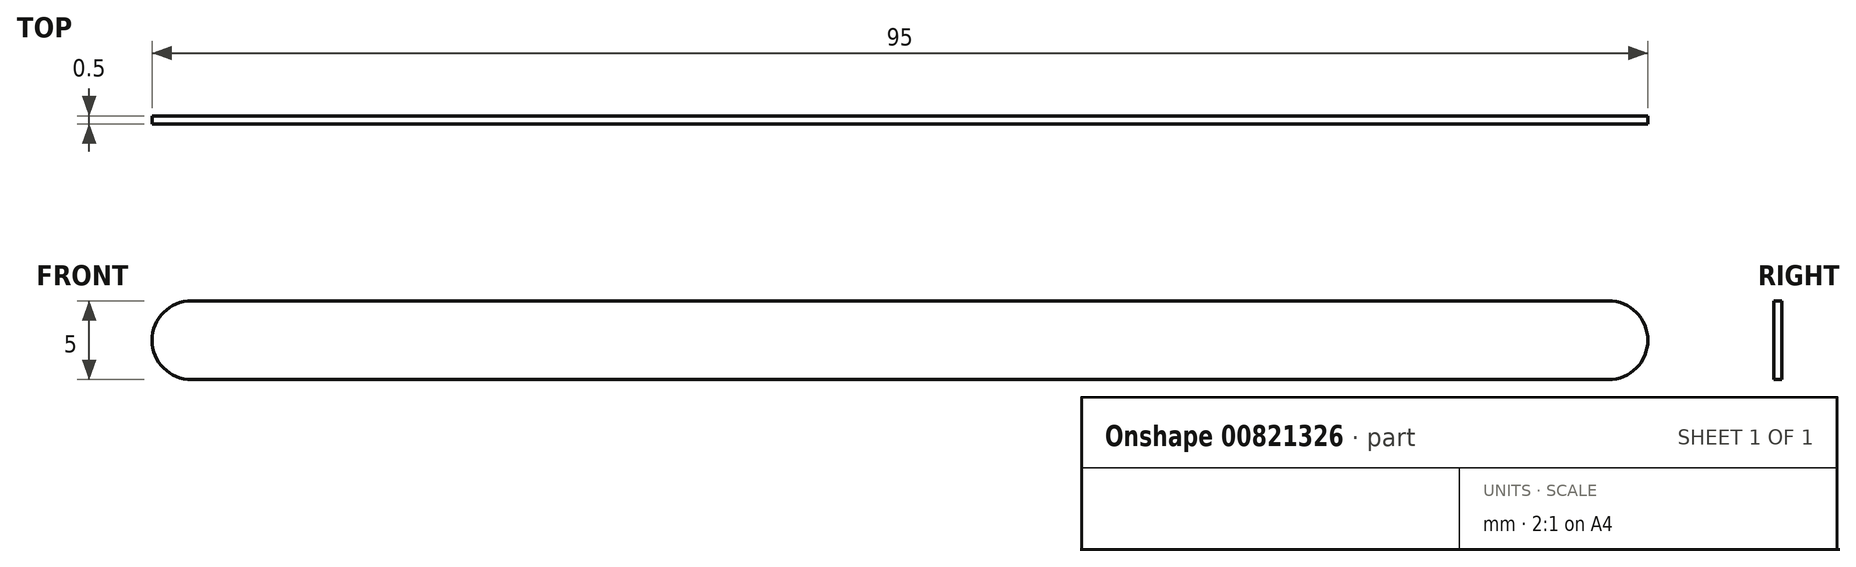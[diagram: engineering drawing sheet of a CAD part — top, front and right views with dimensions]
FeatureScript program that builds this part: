
annotation { "Feature Type Name" : "Feature", "Feature Type Description" : "" }
export const myFeature = defineFeature(function(context is Context, id is Id, definition is map)
    precondition{}
    {
        {
            var Q0;
            Q0=qCreatedBy(makeId("Front.planeOp"),FACE);
            var sketch = newSketch(context, id + "F0", { "sketchPlane" : qUnion([Q0])});
            skLineSegment(sketch, "E0", {"start": v(-26.27, 0) * mm, "end": v(63.73, 0) * mm, "construction": true});
            skArc(sketch, "E1.0.startCap", {"start": v(-26.27, -2.5) * mm, "mid": v(-28.77, 0) * mm, "end": v(-26.27, 2.5) * mm});
            skArc(sketch, "E1.0.endCap", {"start": v(63.73, 2.5) * mm, "mid": v(66.23, 0) * mm, "end": v(63.73, -2.5) * mm});
            skLineSegment(sketch, "E1.0.left", {"start": v(-26.27, 2.5) * mm, "end": v(63.73, 2.5) * mm});
            skLineSegment(sketch, "E1.0.right", {"start": v(-26.27, -2.5) * mm, "end": v(63.73, -2.5) * mm});
            skSolve(sketch);
        }
        {
            var Q0;
            Q0 = qSketchRegion(id + "F0", true);
            extrude(context, id + "F1", {"entities" : qUnion([Q0]), "depth" : .5 * mm, "offsetDistance" : 25 * mm});
        }
    });
